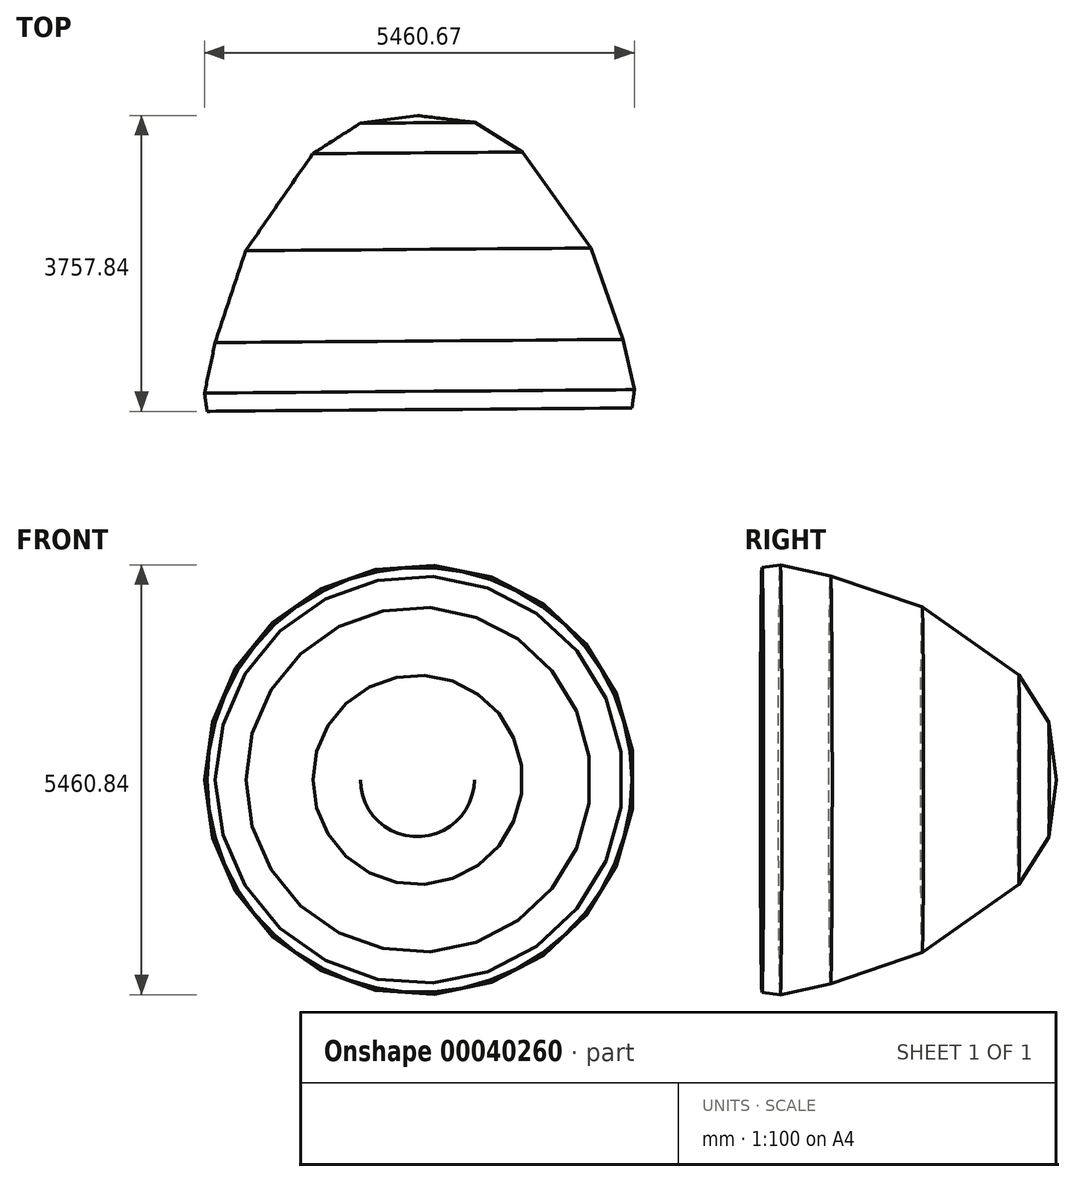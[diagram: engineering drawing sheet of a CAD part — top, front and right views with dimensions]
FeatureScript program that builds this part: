
annotation { "Feature Type Name" : "Feature", "Feature Type Description" : "" }
export const myFeature = defineFeature(function(context is Context, id is Id, definition is map)
    precondition{}
    {
        {
            var Q0;
            Q0=qCreatedBy(makeId("Top.planeOp"),FACE);
            var sketch = newSketch(context, id + "F0", { "sketchPlane" : qUnion([Q0])});
            skLineSegment(sketch, "E0", {"start": v(-2757.71, 3715.66) * mm, "end": v(-2699.66, -3715.66) * mm});
            skLineSegment(sketch, "E1", {"start": v(-2699.66, -3715.66) * mm, "end": v(2699.66, -3715.66) * mm});
            skLineSegment(sketch, "E2", {"start": v(2699.66, -3715.66) * mm, "end": v(2757.71, -3251.2) * mm});
            skLineSegment(sketch, "E3", {"start": v(2757.71, -3251.2) * mm, "end": v(2467.43, -1973.94) * mm});
            skLineSegment(sketch, "E4", {"start": v(2467.43, -1973.94) * mm, "end": v(1654.63, 348.34) * mm});
            skLineSegment(sketch, "E5", {"start": v(1654.63, 348.34) * mm, "end": v(-87.09, 2786.74) * mm});
            skLineSegment(sketch, "E6", {"start": v(-87.09, 2786.74) * mm, "end": v(-1306.29, 3541.49) * mm});
            skLineSegment(sketch, "E7", {"start": v(-1306.29, 3541.49) * mm, "end": v(-2757.71, 3715.66) * mm});
            skSolve(sketch);
        }
        {
            var Q0;
            Q0=makeQuery(id+"F0.imprint","IMPRINT",FACE,{"disambiguationData":[TD([[makeQuery(id+"F0.imprint","IMPRINT",EDGE,{"derivedFrom":sQuery(id+"F0.wireOp",EDGE,"E0")}),1.0]])]});
            var Q1;
            Q1=sQuery(id+"F0.wireOp",EDGE,"E0");
            revolve(context, id + "F1", {"entities" : qUnion([Q0]), "axis" : qUnion([Q1]), "revolveType" : RevolveType.FULL});
        }
        {
            var Q0;
            Q0=makeQuery(id+"F1.opRevolve","SWEPT_BODY",BODY,{"disambiguationData":[OSD([sQuery(id+"F0.wireOp",EDGE,"E0"),sQuery(id+"F0.wireOp",EDGE,"E1"),sQuery(id+"F0.wireOp",EDGE,"E2"),sQuery(id+"F0.wireOp",EDGE,"E3"),sQuery(id+"F0.wireOp",EDGE,"E4"),sQuery(id+"F0.wireOp",EDGE,"E5"),sQuery(id+"F0.wireOp",EDGE,"E6"),sQuery(id+"F0.wireOp",EDGE,"E7")])]});
            var Q1;
            Q1=qCreatedBy(makeId("Origin.pointOp"),VERTEX);
            transform(context, id + "F2", {"entities" : qUnion([Q0]), "transformType" : TransformType.SCALE_UNIFORMLY, "scale" : .5, "makeCopy" : false, "scalePoint" : qUnion([Q1])});
        }
        {
            var Q0;
            Q0=makeQuery(id+"F1.opRevolve","SWEPT_FACE",FACE,{"disambiguationData":[OSD([sQuery(id+"F0.wireOp",EDGE,"E1")])]});
            shell(context, id + "F3", {"entities" : qUnion([Q0]), "thickness" : 2.54 * mm});
        }
    });
